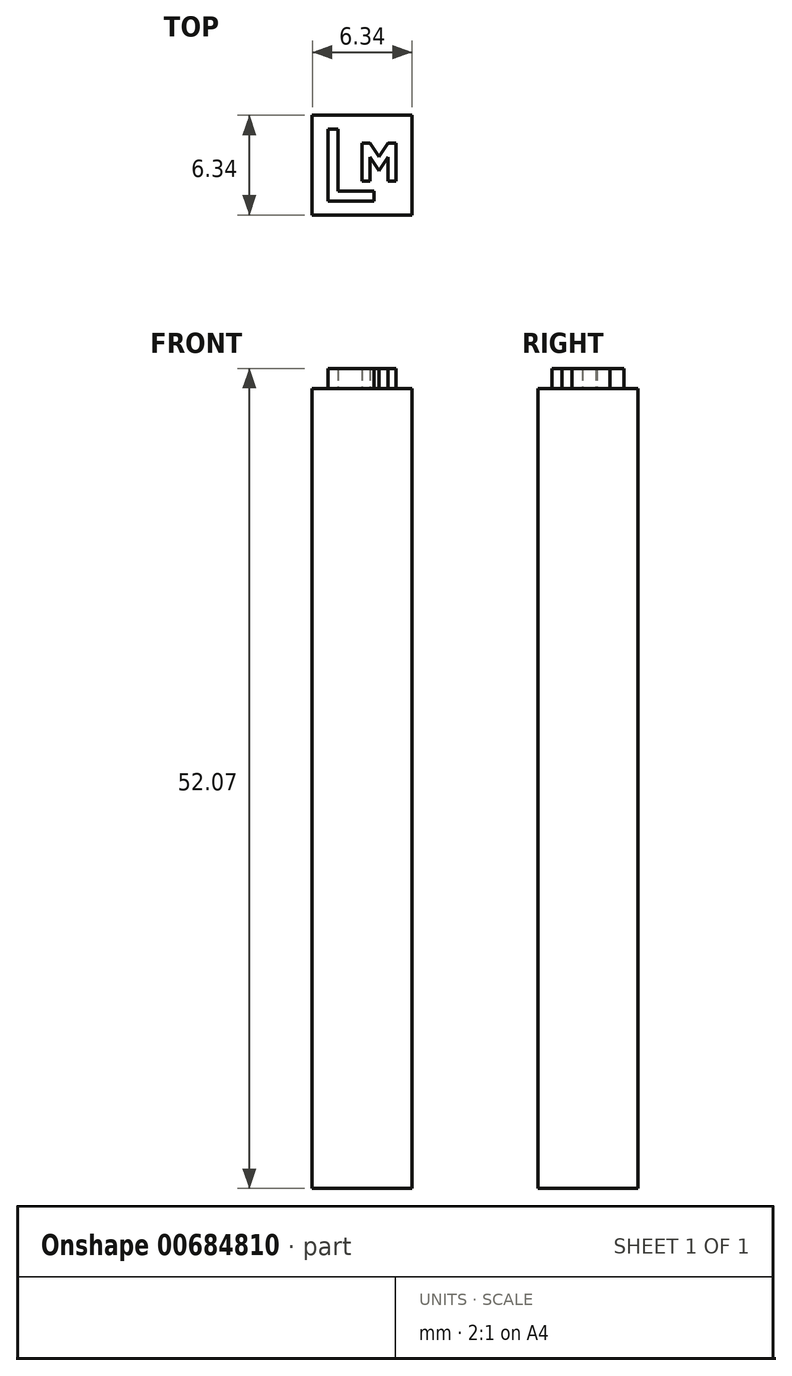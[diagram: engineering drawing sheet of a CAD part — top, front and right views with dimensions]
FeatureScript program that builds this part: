
annotation { "Feature Type Name" : "Feature", "Feature Type Description" : "" }
export const myFeature = defineFeature(function(context is Context, id is Id, definition is map)
    precondition{}
    {
        {
            var Q0;
            Q0=qCreatedBy(makeId("Top.planeOp"),FACE);
            var sketch = newSketch(context, id + "F0", { "sketchPlane" : qUnion([Q0])});
            skLineSegment(sketch, "E0.bottom", {"start": v(3.18, 3.18) * mm, "end": v(-3.18, 3.18) * mm});
            skLineSegment(sketch, "E0.top", {"start": v(3.18, -3.17) * mm, "end": v(-3.18, -3.17) * mm});
            skLineSegment(sketch, "E0.left", {"start": v(3.18, 3.18) * mm, "end": v(3.18, -3.17) * mm});
            skLineSegment(sketch, "E0.right", {"start": v(-3.18, 3.18) * mm, "end": v(-3.18, -3.17) * mm});
            skPoint(sketch, "E0.middle", {"position": v(0, 0) * mm});
            skSolve(sketch);
        }
        {
            var Q0;
            Q0=makeQuery(id+"F0.imprint","IMPRINT",FACE,{"disambiguationData":[TD([[makeQuery(id+"F0.imprint","IMPRINT",EDGE,{"derivedFrom":sQuery(id+"F0.wireOp",EDGE,"E0.bottom")}),1.0]])]});
            extrude(context, id + "F1", {"entities" : qUnion([Q0]), "depth" : 50.8 * mm, "offsetDistance" : 25.4 * mm});
        }
        {
            var Q0;
            Q0=makeQuery(id+"F1.opExtrude","CAP_FACE",FACE,{"disambiguationData":[OSD([sQuery(id+"F0.wireOp",EDGE,"E0.bottom"),sQuery(id+"F0.wireOp",EDGE,"E0.top"),sQuery(id+"F0.wireOp",EDGE,"E0.left"),sQuery(id+"F0.wireOp",EDGE,"E0.right")])],"isStart":false});
            var sketch = newSketch(context, id + "F2", { "sketchPlane" : qUnion([Q0])});
            skLineSegment(sketch, "E1", {"start": v(0, 0) * mm, "end": v(0, 1.4) * mm});
            skLineSegment(sketch, "E2", {"start": v(0, 0) * mm, "end": v(0, -1.02) * mm});
            skLineSegment(sketch, "E3", {"start": v(0, -1.02) * mm, "end": v(0.5, -1.02) * mm});
            skLineSegment(sketch, "E4", {"start": v(0.5, -1.02) * mm, "end": v(0.5, 0.5) * mm});
            skLineSegment(sketch, "E5", {"start": v(0.5, 0.5) * mm, "end": v(1.08, -0.36) * mm});
            skLineSegment(sketch, "E6", {"start": v(1.08, -0.36) * mm, "end": v(1.65, 0.5) * mm});
            skLineSegment(sketch, "E7", {"start": v(1.65, 0.5) * mm, "end": v(1.65, -1.02) * mm});
            skLineSegment(sketch, "E8", {"start": v(1.65, -1.02) * mm, "end": v(2.16, -1.02) * mm});
            skLineSegment(sketch, "E9", {"start": v(2.16, -1.02) * mm, "end": v(2.16, 1.4) * mm});
            skLineSegment(sketch, "E10", {"start": v(2.16, 1.4) * mm, "end": v(1.65, 1.4) * mm});
            skLineSegment(sketch, "E11", {"start": v(1.65, 1.4) * mm, "end": v(1.08, 0.55) * mm});
            skLineSegment(sketch, "E12", {"start": v(1.08, 0.55) * mm, "end": v(0.5, 1.4) * mm});
            skLineSegment(sketch, "E13", {"start": v(0.5, 1.4) * mm, "end": v(0, 1.4) * mm});
            skLineSegment(sketch, "E14", {"start": v(-2.16, 2.29) * mm, "end": v(-2.16, -2.29) * mm});
            skLineSegment(sketch, "E15", {"start": v(-2.16, 2.29) * mm, "end": v(-1.52, 2.29) * mm});
            skLineSegment(sketch, "E16", {"start": v(-1.52, 2.29) * mm, "end": v(-1.52, -1.65) * mm});
            skLineSegment(sketch, "E17", {"start": v(-1.52, -1.65) * mm, "end": v(0.76, -1.65) * mm});
            skLineSegment(sketch, "E18", {"start": v(0.76, -1.65) * mm, "end": v(0.76, -2.29) * mm});
            skLineSegment(sketch, "E19", {"start": v(0.76, -2.29) * mm, "end": v(-2.16, -2.29) * mm});
            skSolve(sketch);
        }
        {
            var Q0;
            Q0=makeQuery(id+"F2.imprint","IMPRINT",FACE,{"disambiguationData":[TD([[makeQuery(id+"F2.imprint","IMPRINT",EDGE,{"derivedFrom":sQuery(id+"F2.wireOp",EDGE,"E1")}),-1.0]])]});
            var Q1;
            Q1=makeQuery(id+"F2.imprint","IMPRINT",FACE,{"disambiguationData":[TD([[makeQuery(id+"F2.imprint","IMPRINT",EDGE,{"derivedFrom":sQuery(id+"F2.wireOp",EDGE,"E14")}),1.0]])]});
            extrude(context, id + "F3", {"entities" : qUnion([Q0, Q1]), "operationType" : NewBodyOperationType.ADD, "depth" : 1.27 * mm, "offsetDistance" : 25.4 * mm});
        }
    });
